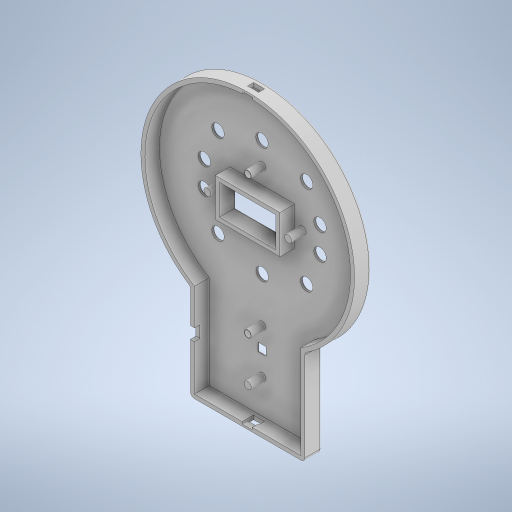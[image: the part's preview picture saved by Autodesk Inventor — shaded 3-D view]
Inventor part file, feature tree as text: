
AUTODESK INVENTOR PART (.ipt)
format: ipt  version: 2024 (Build 280153000, 153)  size: 547,840 bytes
history: native  units: mm
features: sketch x16, extrude x15, fillet x4, other x1
ambient origin geometry x8: Origin, YZ Plane, XZ Plane, XY Plane, X Axis, Y Axis, Z Axis, Center Point
bodies: Body1 (feature_tree)
feature tree (36):
  extrude  "Extrusion2"  Depth=102.0mm
  sketch  "Esquisse2"
  extrude  "Extrusion5"  Depth=26.4mm
  sketch  "Esquisse4"
  sketch  "Esquisse5"
  extrude  "Extrusion6"  Depth=90.0mm
  extrude  "Extrusion7"  Depth=26.4mm
  extrude  "Extrusion8"  Depth=1.0mm TaperAngle=0.0deg
  extrude  "Extrusion9"  Depth=3.5mm
  fillet  "Congé1"  Radius=39.1mm
  fillet  "Congé2"  Radius=26.4mm
  extrude  "Extrusion10"  Depth=3.5mm
  sketch  "Esquisse10"
  extrude  "Extrusion11"  Depth=107.68mm
  extrude  "Extrusion12"  Depth=26.4mm
  fillet  "Congé3"  Radius=7.195mm
  extrude  "Extrusion13"  Depth=3.0mm
  extrude  "Extrusion14"  Depth=3.0mm
  sketch  "Esquisse18"
  other  "Plan de construction7"
  extrude  "Extrusion16"  Depth=3.0mm TaperAngle=0.0deg
  extrude  "Extrusion17"  Depth=3.0mm TaperAngle=0.0deg
  extrude  "Extrusion18"  Depth=3.5mm
  fillet  "Congé4"  Radius=17.0mm
  extrude  "Extrusion19"  Depth=3.5mm
  sketch  "Esquisse1"
  sketch  "Esquisse6"
  sketch  "Esquisse8"
  sketch  "Esquisse9"
  sketch  "Esquisse11"
  sketch  "Esquisse12"
  sketch  "Esquisse13"
  sketch  "Esquisse14"
  sketch  "Esquisse19"
  sketch  "Esquisse20"
  sketch  "Esquisse21"
